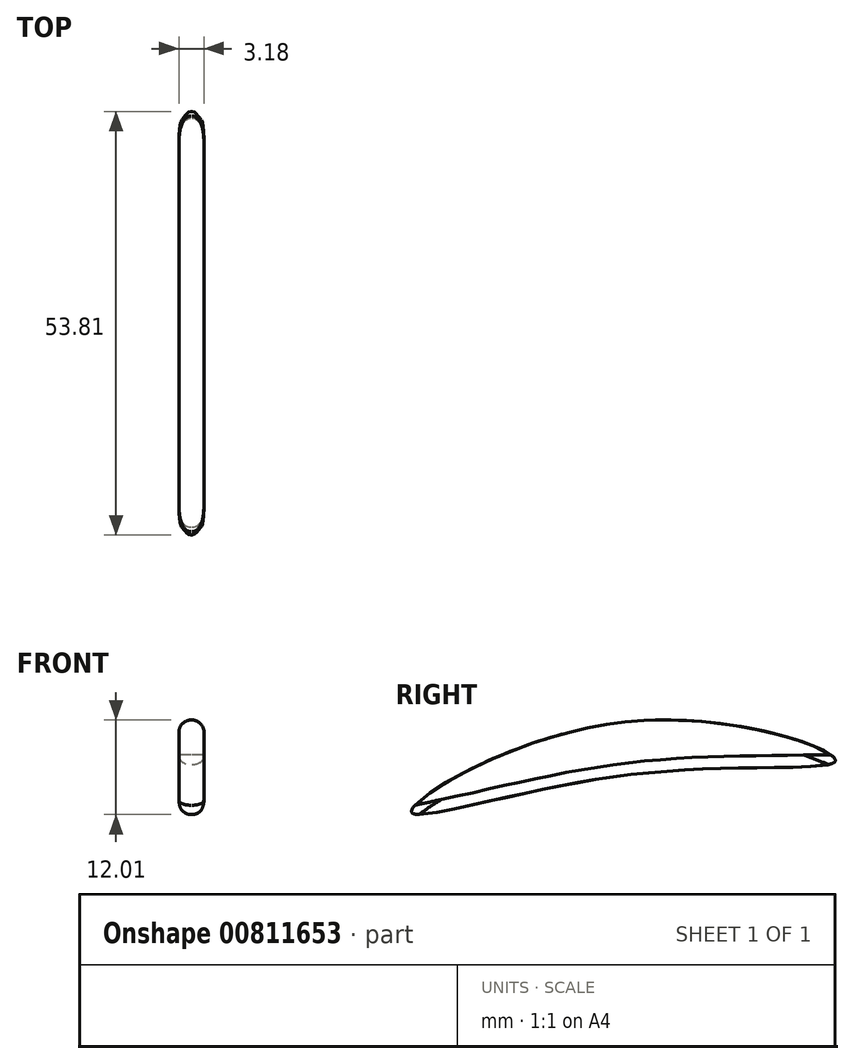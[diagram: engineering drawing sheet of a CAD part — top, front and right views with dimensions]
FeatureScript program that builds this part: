
annotation { "Feature Type Name" : "Feature", "Feature Type Description" : "" }
export const myFeature = defineFeature(function(context is Context, id is Id, definition is map)
    precondition{}
    {
        {
            var Q0;
            Q0=qCreatedBy(makeId("Right.planeOp"),FACE);
            var sketch = newSketch(context, id + "F0", { "sketchPlane" : qUnion([Q0])});
            skFitSpline(sketch, "E0", {"points": [v(-74.99, 10.52) * mm, v(-48.25, 21.9) * mm, v(-21.18, 17.07) * mm, v(-47.11, 15.26) * mm, v(-74.99, 10.52) * mm]});
            skSolve(sketch);
        }
        {
            var Q0;
            Q0=makeQuery(id+"F0.imprint","IMPRINT",FACE,{"disambiguationData":[TD([[makeQuery(id+"F0.imprint","IMPRINT",EDGE,{"derivedFrom":sQuery(id+"F0.wireOp",EDGE,"E0")}),-1.0]])]});
            extrude(context, id + "F1", {"entities" : qUnion([Q0]), "depth" : 3.17 * mm, "offsetDistance" : 25.4 * mm});
        }
        {
            var Q0;
            Q0=makeQuery(id+"F1.opExtrude","CAP_EDGE",EDGE,{"disambiguationData":[OSD([sQuery(id+"F0.wireOp",EDGE,"E0")])],"isStart":false});
            var Q1;
            Q1=makeQuery(id+"F1.opExtrude","CAP_EDGE",EDGE,{"disambiguationData":[OSD([sQuery(id+"F0.wireOp",EDGE,"E0")])],"isStart":true});
            fillet(context, id + "F2", {"entities" : qUnion([Q0, Q1]), "radius" : 1.52 * mm, "tangentPropagation" : true, "allowEdgeOverflow" : false});
        }
    });
